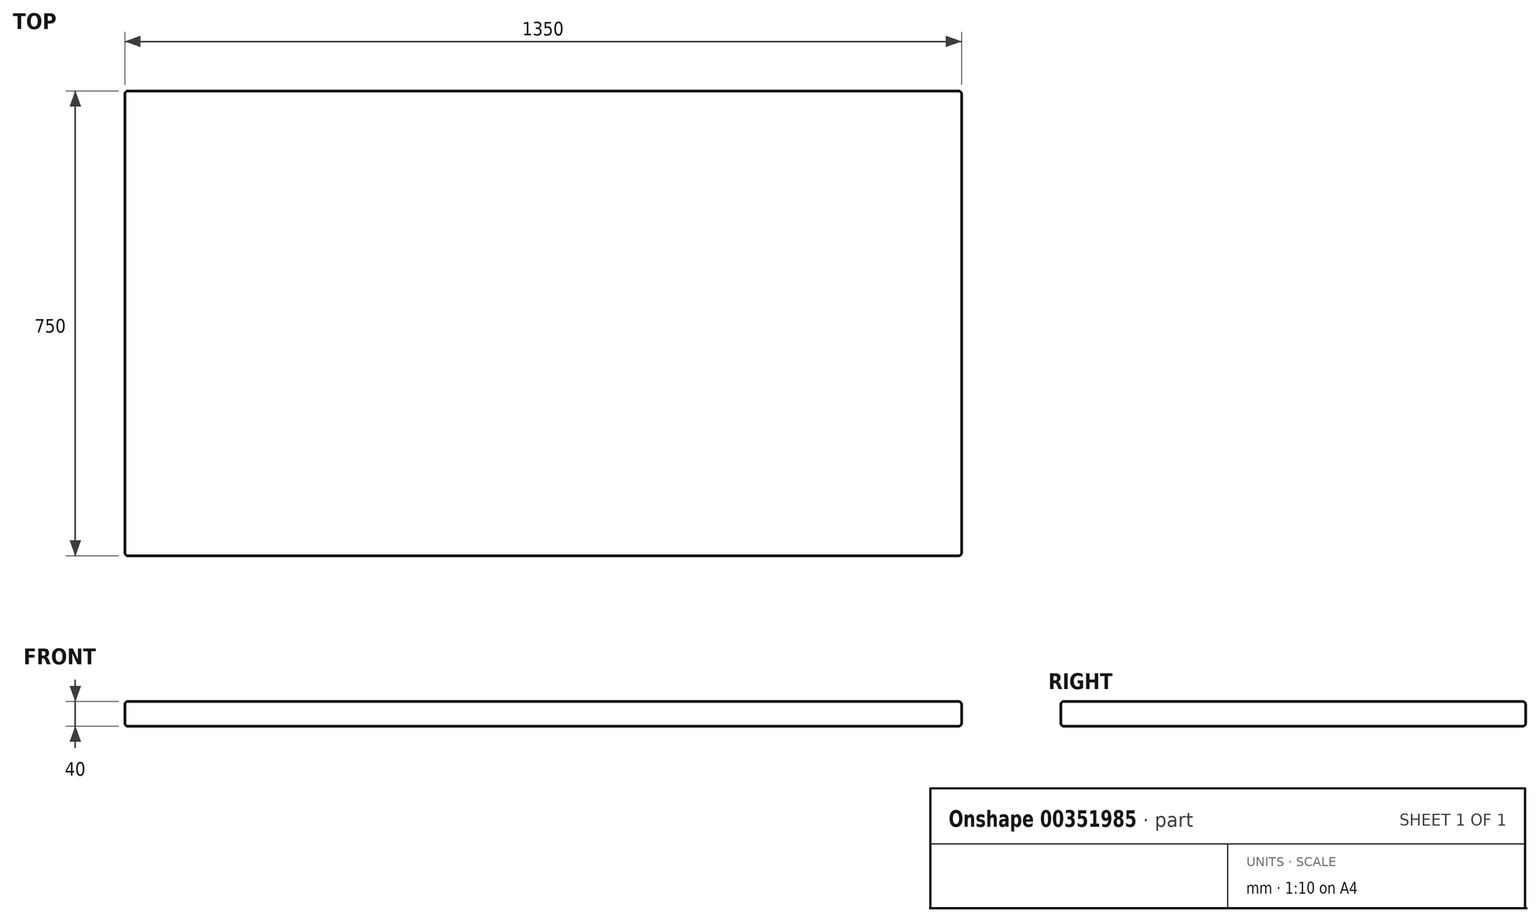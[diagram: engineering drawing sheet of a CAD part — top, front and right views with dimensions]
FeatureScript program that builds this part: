
annotation { "Feature Type Name" : "Feature", "Feature Type Description" : "" }
export const myFeature = defineFeature(function(context is Context, id is Id, definition is map)
    precondition{}
    {
        {
            var Q0;
            Q0=qCreatedBy(makeId("Top.planeOp"),FACE);
            var sketch = newSketch(context, id + "F0", { "sketchPlane" : qUnion([Q0])});
            skLineSegment(sketch, "E0.bottom", {"start": v(675, 375) * mm, "end": v(-675, 375) * mm});
            skLineSegment(sketch, "E0.top", {"start": v(675, -375) * mm, "end": v(-675, -375) * mm});
            skLineSegment(sketch, "E0.left", {"start": v(675, 375) * mm, "end": v(675, -375) * mm});
            skLineSegment(sketch, "E0.right", {"start": v(-675, 375) * mm, "end": v(-675, -375) * mm});
            skPoint(sketch, "E0.middle", {"position": v(0, 0) * mm});
            skSolve(sketch);
        }
        {
            var Q0;
            Q0=makeQuery(id+"F0.imprint","IMPRINT",FACE,{"disambiguationData":[TD([[makeQuery(id+"F0.imprint","IMPRINT",EDGE,{"derivedFrom":sQuery(id+"F0.wireOp",EDGE,"E0.bottom")}),1.0]])]});
            extrude(context, id + "F1", {"entities" : qUnion([Q0]), "depth" : 40 * mm});
        }
        {
            var Q0;
            Q0=makeQuery(id+"F1.opExtrude","CAP_FACE",FACE,{"disambiguationData":[OSD([sQuery(id+"F0.wireOp",EDGE,"E0.bottom"),sQuery(id+"F0.wireOp",EDGE,"E0.top"),sQuery(id+"F0.wireOp",EDGE,"E0.left"),sQuery(id+"F0.wireOp",EDGE,"E0.right")])],"isStart":false});
            var Q1;
            Q1=makeQuery(id+"F1.opExtrude","CAP_FACE",FACE,{"disambiguationData":[OSD([sQuery(id+"F0.wireOp",EDGE,"E0.bottom"),sQuery(id+"F0.wireOp",EDGE,"E0.top"),sQuery(id+"F0.wireOp",EDGE,"E0.left"),sQuery(id+"F0.wireOp",EDGE,"E0.right")])],"isStart":true});
            var Q2;
            Q2=makeQuery(id+"F1.opExtrude","SWEPT_FACE",FACE,{"disambiguationData":[OSD([sQuery(id+"F0.wireOp",EDGE,"E0.left")])]});
            var Q3;
            Q3=makeQuery(id+"F1.opExtrude","SWEPT_FACE",FACE,{"disambiguationData":[OSD([sQuery(id+"F0.wireOp",EDGE,"E0.right")])]});
            fillet(context, id + "F2", {"entities" : qUnion([Q0, Q1, Q2, Q3]), "radius" : 5 * mm, "tangentPropagation" : true, "allowEdgeOverflow" : false});
        }
    });
